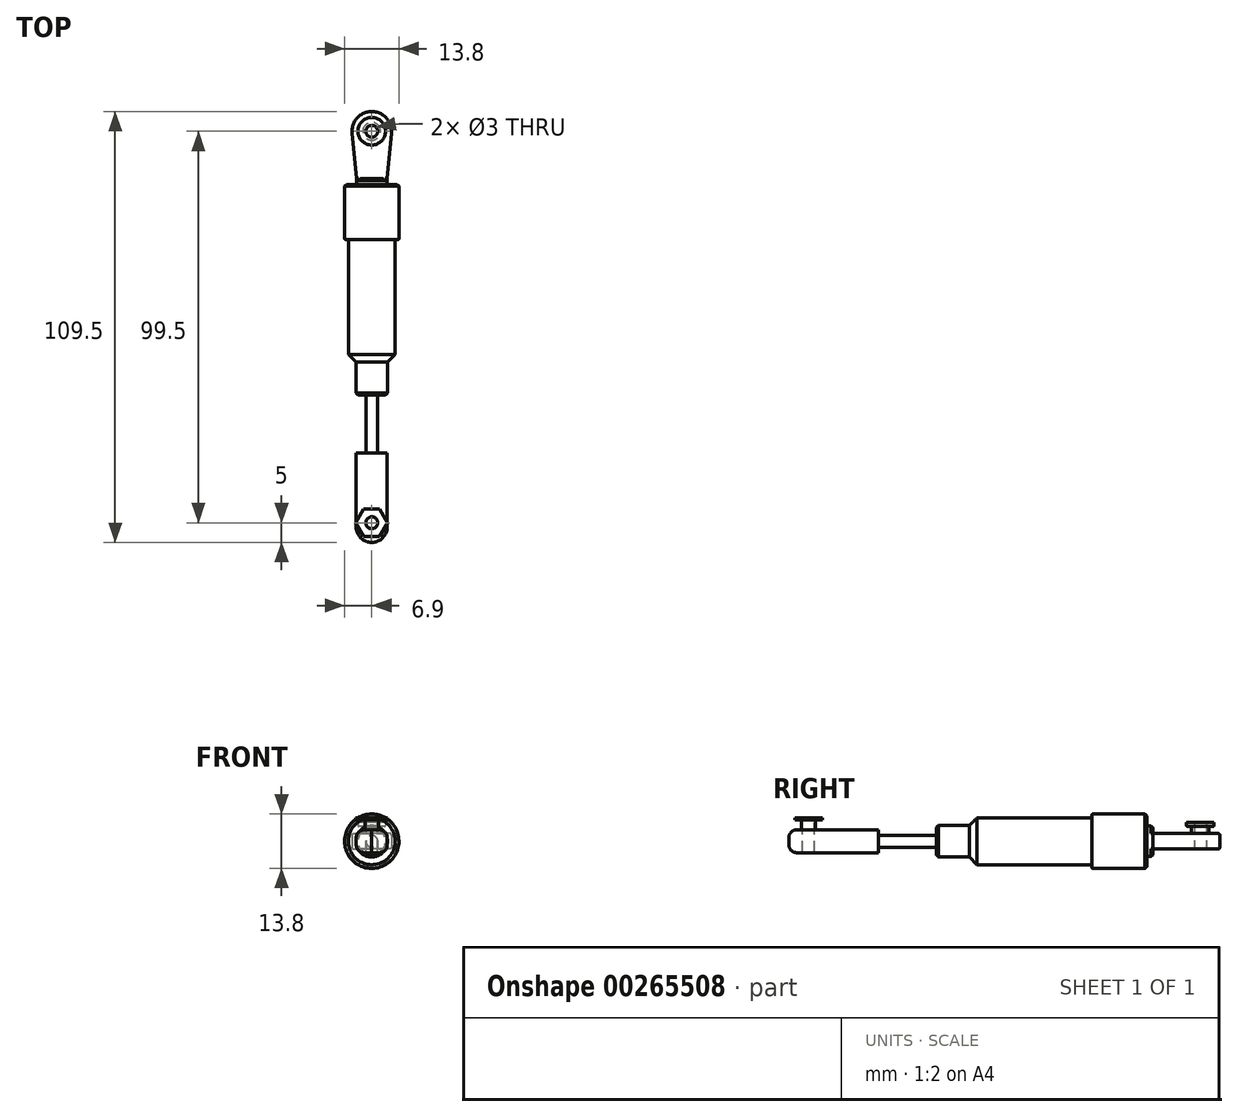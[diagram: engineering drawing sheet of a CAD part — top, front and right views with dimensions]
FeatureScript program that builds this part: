
annotation { "Feature Type Name" : "Feature", "Feature Type Description" : "" }
export const myFeature = defineFeature(function(context is Context, id is Id, definition is map)
    precondition{}
    {
        {
            var Q0;
            Q0=qCreatedBy(makeId("Front.planeOp"),FACE);
            var sketch = newSketch(context, id + "F0", { "sketchPlane" : qUnion([Q0])});
            skCircle(sketch, "E0", {"center": v(0, 0) * mm, "radius": 6.9 * mm});
            skSolve(sketch);
        }
        {
            var Q0;
            Q0=makeQuery(id+"F0.imprint","IMPRINT",FACE,{"disambiguationData":[TD([[makeQuery(id+"F0.imprint","IMPRINT",EDGE,{"derivedFrom":sQuery(id+"F0.wireOp",EDGE,"E0")}),1.0]])]});
            extrude(context, id + "F1", {"entities" : qUnion([Q0]), "depth" : 14 * mm});
        }
        {
            var Q0;
            Q0=makeQuery(id+"F1.opExtrude","CAP_FACE",FACE,{"disambiguationData":[OSD([sQuery(id+"F0.wireOp",EDGE,"E0")])],"isStart":false});
            var sketch = newSketch(context, id + "F2", { "sketchPlane" : qUnion([Q0])});
            skCircle(sketch, "E1", {"center": v(0, 0) * mm, "radius": 5.95 * mm});
            skSolve(sketch);
        }
        {
            var Q0;
            Q0=makeQuery(id+"F2.imprint","IMPRINT",FACE,{"disambiguationData":[TD([[makeQuery(id+"F2.imprint","IMPRINT",EDGE,{"derivedFrom":sQuery(id+"F2.wireOp",EDGE,"E1")}),1.0]])]});
            extrude(context, id + "F3", {"entities" : qUnion([Q0]), "operationType" : NewBodyOperationType.ADD, "depth" : 32 * mm});
        }
        {
            var Q0;
            Q0=makeQuery(id+"F3.opExtrude","CAP_FACE",FACE,{"disambiguationData":[OSD([sQuery(id+"F2.wireOp",EDGE,"E1")])],"isStart":false});
            var sketch = newSketch(context, id + "F4", { "sketchPlane" : qUnion([Q0])});
            skCircle(sketch, "E2", {"center": v(0, 0) * mm, "radius": 4 * mm});
            skSolve(sketch);
        }
        {
            var Q0;
            Q0=makeQuery(id+"F4.imprint","IMPRINT",FACE,{"disambiguationData":[TD([[makeQuery(id+"F4.imprint","IMPRINT",EDGE,{"derivedFrom":sQuery(id+"F4.wireOp",EDGE,"E2")}),1.0]])]});
            extrude(context, id + "F5", {"entities" : qUnion([Q0]), "operationType" : NewBodyOperationType.ADD, "depth" : 7.5 * mm});
        }
        {
            var Q0;
            Q0=makeQuery(id+"F3.opExtrude","CAP_EDGE",EDGE,{"disambiguationData":[OSD([sQuery(id+"F2.wireOp",EDGE,"E1")])],"isStart":false});
            chamfer(context, id + "F6", {"entities" : qUnion([Q0]), "width" : 2.8 * mm, "tangentPropagation" : true});
        }
        {
            var Q0;
            Q0=makeQuery(id+"F5.opExtrude","CAP_FACE",FACE,{"disambiguationData":[OSD([sQuery(id+"F4.wireOp",EDGE,"E2")])],"isStart":false});
            var sketch = newSketch(context, id + "F7", { "sketchPlane" : qUnion([Q0])});
            skCircle(sketch, "E3", {"center": v(0, 0) * mm, "radius": 1.5 * mm});
            skSolve(sketch);
        }
        {
            var Q0;
            Q0=makeQuery(id+"F7.imprint","IMPRINT",FACE,{"disambiguationData":[TD([[makeQuery(id+"F7.imprint","IMPRINT",EDGE,{"derivedFrom":sQuery(id+"F7.wireOp",EDGE,"E3")}),1.0]])]});
            extrude(context, id + "F8", {"entities" : qUnion([Q0]), "operationType" : NewBodyOperationType.ADD, "depth" : 14.8 * mm});
        }
        {
            var Q0;
            Q0=makeQuery(id+"F8.opExtrude","CAP_FACE",FACE,{"disambiguationData":[OSD([sQuery(id+"F7.wireOp",EDGE,"E3")])],"isStart":false});
            var sketch = newSketch(context, id + "F9", { "sketchPlane" : qUnion([Q0])});
            skLineSegment(sketch, "E4.bottom", {"start": v(-3.95, -2.9) * mm, "end": v(3.95, -2.9) * mm});
            skLineSegment(sketch, "E4.top", {"start": v(-3.95, 2.9) * mm, "end": v(3.95, 2.9) * mm});
            skLineSegment(sketch, "E4.left", {"start": v(-3.95, -2.9) * mm, "end": v(-3.95, 2.9) * mm});
            skLineSegment(sketch, "E4.right", {"start": v(3.95, -2.9) * mm, "end": v(3.95, 2.9) * mm});
            skPoint(sketch, "E4.middle", {"position": v(0, 0) * mm});
            skSolve(sketch);
        }
        {
            var Q0;
            Q0=makeQuery(id+"F9.imprint","IMPRINT",FACE,{"disambiguationData":[TD([[makeQuery(id+"F9.imprint","IMPRINT",EDGE,{"derivedFrom":sQuery(id+"F9.wireOp",EDGE,"E4.bottom")}),1.0]])]});
            var Q1;
            Q1=makeQuery(id+"F9.imprint","IMPRINT",FACE,{"disambiguationData":[TD([[makeQuery(id+"F9.imprint","IMPRINT",EDGE,{"derivedFrom":makeQuery(id+"F8.opExtrude","CAP_EDGE",EDGE,{"disambiguationData":[OSD([sQuery(id+"F7.wireOp",EDGE,"E3")])],"isStart":false})}),1.0]])]});
            extrude(context, id + "F10", {"entities" : qUnion([Q0, Q1]), "operationType" : NewBodyOperationType.ADD, "depth" : 22.7 * mm});
        }
        {
            var Q0;
            Q0=makeQuery(id+"F10.opExtrude","CAP_EDGE",EDGE,{"disambiguationData":[OSD([sQuery(id+"F9.wireOp",EDGE,"E4.left")])],"isStart":false});
            var Q1;
            Q1=makeQuery(id+"F10.opExtrude","CAP_EDGE",EDGE,{"disambiguationData":[OSD([sQuery(id+"F9.wireOp",EDGE,"E4.right")])],"isStart":false});
            fillet(context, id + "F11", {"entities" : qUnion([Q0, Q1]), "radius" : 4 * mm, "tangentPropagation" : true, "allowEdgeOverflow" : false});
        }
        {
            var Q0;
            Q0=makeQuery(id+"F10.opExtrude","SWEPT_EDGE",EDGE,{"disambiguationData":[OSD([sQuery(id+"F9.wireOp",EDGE,"E4.top"),sQuery(id+"F9.wireOp",EDGE,"E4.left")])]});
            var Q1;
            Q1=makeQuery(id+"F10.opExtrude","SWEPT_EDGE",EDGE,{"disambiguationData":[OSD([sQuery(id+"F9.wireOp",EDGE,"E4.top"),sQuery(id+"F9.wireOp",EDGE,"E4.right")])]});
            var Q2;
            Q2=makeQuery(id+"F10.opExtrude","SWEPT_EDGE",EDGE,{"disambiguationData":[OSD([sQuery(id+"F9.wireOp",EDGE,"E4.bottom"),sQuery(id+"F9.wireOp",EDGE,"E4.right")])]});
            var Q3;
            Q3=makeQuery(id+"F10.opExtrude","SWEPT_EDGE",EDGE,{"disambiguationData":[OSD([sQuery(id+"F9.wireOp",EDGE,"E4.bottom"),sQuery(id+"F9.wireOp",EDGE,"E4.left")])]});
            fillet(context, id + "F12", {"entities" : qUnion([Q0, Q1, Q2, Q3]), "radius" : 2 * mm, "tangentPropagation" : true, "allowEdgeOverflow" : false});
        }
        {
            var Q0;
            Q0=makeQuery(id+"F10.opExtrude","SWEPT_FACE",FACE,{"disambiguationData":[OSD([sQuery(id+"F9.wireOp",EDGE,"E4.top")])]});
            var sketch = newSketch(context, id + "F13", { "sketchPlane" : qUnion([Q0])});
            skLineSegment(sketch, "E5", {"start": v(0, -86) * mm, "end": v(0, -91) * mm, "construction": true});
            skCircle(sketch, "E6", {"center": v(0, -86) * mm, "radius": 1.5 * mm});
            skCircle(sketch, "E7", {"center": v(0, -86) * mm, "radius": 1.75 * mm});
            skSolve(sketch);
        }
        {
            var Q0;
            Q0=makeQuery(id+"F13.imprint","IMPRINT",FACE,{"disambiguationData":[TD([[makeQuery(id+"F13.imprint","IMPRINT",EDGE,{"derivedFrom":sQuery(id+"F13.wireOp",EDGE,"E6")}),1.0]])]});
            extrude(context, id + "F14", {"entities" : qUnion([Q0]), "operationType" : NewBodyOperationType.REMOVE, "oppositeDirection" : true, "depth" : 10 * mm});
        }
        {
            var Q0;
            Q0=makeQuery(id+"F13.imprint","IMPRINT",FACE,{"disambiguationData":[TD([[makeQuery(id+"F13.imprint","IMPRINT",EDGE,{"derivedFrom":sQuery(id+"F13.wireOp",EDGE,"E6")}),-1.0]])]});
            var Q1;
            Q1=sQuery(id+"F13.wireOp",EDGE,"E7");
            var Q2;
            Q2=sQuery(id+"F13.wireOp",EDGE,"E6");
            extrude(context, id + "F15", {"entities" : qUnion([Q0]), "operationType" : NewBodyOperationType.ADD, "surfaceEntities" : qUnion([Q1, Q2]), "depth" : 2.5 * mm});
        }
        {
            var Q0;
            Q0=makeQuery(id+"F15.opExtrude","CAP_FACE",FACE,{"disambiguationData":[OSD([sQuery(id+"F13.wireOp",EDGE,"E6"),sQuery(id+"F13.wireOp",EDGE,"E7")])],"isStart":false});
            var sketch = newSketch(context, id + "F16", { "sketchPlane" : qUnion([Q0])});
            skCircle(sketch, "E8.cCircle", {"center": v(0, -86) * mm, "radius": 3.5 * mm, "construction": true});
            skLineSegment(sketch, "E8.0", {"start": v(2.02, -89.5) * mm, "end": v(-2.02, -89.5) * mm});
            skLineSegment(sketch, "E8.1", {"start": v(-2.02, -89.5) * mm, "end": v(-4.04, -86) * mm});
            skLineSegment(sketch, "E8.2", {"start": v(-4.04, -86) * mm, "end": v(-2.02, -82.5) * mm});
            skLineSegment(sketch, "E8.3", {"start": v(-2.02, -82.5) * mm, "end": v(2.02, -82.5) * mm});
            skLineSegment(sketch, "E8.4", {"start": v(2.02, -82.5) * mm, "end": v(4.04, -86) * mm});
            skLineSegment(sketch, "E8.5", {"start": v(4.04, -86) * mm, "end": v(2.02, -89.5) * mm});
            skPoint(sketch, "E8.0.midPoint", {"position": v(0, -89.5) * mm});
            skCircle(sketch, "E9", {"center": v(0, -86) * mm, "radius": 1.5 * mm});
            skSolve(sketch);
        }
        {
            var Q0;
            Q0 = qSketchRegion(id + "F16", true);
            extrude(context, id + "F17", {"entities" : qUnion([Q0]), "operationType" : NewBodyOperationType.ADD, "depth" : 0.5 * mm});
        }
        {
            var Q0;
            Q0=makeQuery(id+"F1.opExtrude","CAP_FACE",FACE,{"disambiguationData":[OSD([sQuery(id+"F0.wireOp",EDGE,"E0")])],"isStart":true});
            var sketch = newSketch(context, id + "F18", { "sketchPlane" : qUnion([Q0])});
            skCircle(sketch, "E10", {"center": v(0, 0) * mm, "radius": 3.9 * mm});
            skSolve(sketch);
        }
        {
            var Q0;
            Q0=makeQuery(id+"F18.imprint","IMPRINT",FACE,{"disambiguationData":[TD([[makeQuery(id+"F18.imprint","IMPRINT",EDGE,{"derivedFrom":sQuery(id+"F18.wireOp",EDGE,"E10")}),1.0]])]});
            extrude(context, id + "F19", {"entities" : qUnion([Q0]), "operationType" : NewBodyOperationType.ADD, "depth" : 1.5 * mm});
        }
        {
            var Q0;
            Q0=qCreatedBy(makeId("Top.planeOp"),FACE);
            var sketch = newSketch(context, id + "F20", { "sketchPlane" : qUnion([Q0])});
            skLineSegment(sketch, "E11", {"start": v(0, 0) * mm, "end": v(0, 13.5) * mm, "construction": true});
            skCircle(sketch, "E12", {"center": v(0, 13.5) * mm, "radius": 5 * mm});
            skLineSegment(sketch, "E13.bottom", {"start": v(-3.9, 0) * mm, "end": v(3.9, 0) * mm});
            skLineSegment(sketch, "E13.top", {"start": v(-3.9, 1.5) * mm, "end": v(3.9, 1.5) * mm});
            skLineSegment(sketch, "E13.left", {"start": v(-3.9, 0) * mm, "end": v(-3.9, 1.5) * mm});
            skLineSegment(sketch, "E13.right", {"start": v(3.9, 0) * mm, "end": v(3.9, 1.5) * mm});
            skLineSegment(sketch, "E14", {"start": v(-3.9, 0) * mm, "end": v(3.9, 0) * mm, "construction": true});
            skLineSegment(sketch, "E15", {"start": v(-4.98, 13.03) * mm, "end": v(-3.9, 1.5) * mm});
            skLineSegment(sketch, "E16.MirrorCS", {"start": v(4.98, 13.03) * mm, "end": v(3.9, 1.5) * mm});
            skSolve(sketch);
        }
        {
            var Q0;
            {var subQ0=sQuery(id+"F20.wireOp",EDGE,"E12");var subQ1=makeQuery(id+"F20.imprint","INTERSECT",VERTEX,{"derivedFrom":[subQ0,sQuery(id+"F20.wireOp",EDGE,"E15")]});Q0=makeQuery(id+"F20.imprint","IMPRINT",FACE,{"disambiguationData":[TD([[makeQuery(id+"F20.imprint","IMPRINT",EDGE,{"disambiguationData":[TD([[subQ1,-1.0]])],"derivedFrom":subQ0}),1.0]])]});}
            var Q1;
            Q1=makeQuery(id+"F20.imprint","IMPRINT",FACE,{"disambiguationData":[TD([[makeQuery(id+"F20.imprint","IMPRINT",EDGE,{"derivedFrom":sQuery(id+"F20.wireOp",EDGE,"E13.top")}),1.0]])]});
            extrude(context, id + "F21", {"entities" : qUnion([Q0, Q1]), "operationType" : NewBodyOperationType.ADD, "depth" : 4 * mm, "symmetric" : true});
        }
        {
            var Q0;
            Q0=makeQuery(id+"F21.opExtrude","CAP_FACE",FACE,{"disambiguationData":[OSD([sQuery(id+"F20.wireOp",EDGE,"E12"),sQuery(id+"F20.wireOp",EDGE,"E13.top"),sQuery(id+"F20.wireOp",EDGE,"E15"),sQuery(id+"F20.wireOp",EDGE,"E16.MirrorCS")])],"isStart":false});
            var sketch = newSketch(context, id + "F22", { "sketchPlane" : qUnion([Q0])});
            skCircle(sketch, "E17", {"center": v(0, 13.5) * mm, "radius": 1.5 * mm});
            skCircle(sketch, "E18", {"center": v(0, 13.5) * mm, "radius": 2.25 * mm});
            skSolve(sketch);
        }
        {
            var Q0;
            Q0=makeQuery(id+"F22.imprint","IMPRINT",FACE,{"disambiguationData":[TD([[makeQuery(id+"F22.imprint","IMPRINT",EDGE,{"derivedFrom":sQuery(id+"F22.wireOp",EDGE,"E17")}),-1.0]])]});
            extrude(context, id + "F23", {"entities" : qUnion([Q0]), "operationType" : NewBodyOperationType.ADD, "depth" : 1.8 * mm});
        }
        {
            var Q0;
            Q0=makeQuery(id+"F23.boolean.opBoolean","SPLIT",FACE,{"disambiguationData":[TD([makeQuery(id+"F23.opExtrude","SWEPT_FACE",FACE,{"disambiguationData":[OSD([sQuery(id+"F22.wireOp",EDGE,"E17")])]})])],"derivedFrom":makeQuery(id+"F21.opExtrude","CAP_FACE",FACE,{"disambiguationData":[OSD([sQuery(id+"F20.wireOp",EDGE,"E12"),sQuery(id+"F20.wireOp",EDGE,"E13.top"),sQuery(id+"F20.wireOp",EDGE,"E15"),sQuery(id+"F20.wireOp",EDGE,"E16.MirrorCS")])],"isStart":false})});
            extrude(context, id + "F24", {"entities" : qUnion([Q0]), "operationType" : NewBodyOperationType.REMOVE, "oppositeDirection" : true, "depth" : 5 * mm});
        }
        {
            var Q0;
            Q0=makeQuery(id+"F23.opExtrude","CAP_FACE",FACE,{"disambiguationData":[OSD([sQuery(id+"F22.wireOp",EDGE,"E17"),sQuery(id+"F22.wireOp",EDGE,"E18")])],"isStart":false});
            var sketch = newSketch(context, id + "F25", { "sketchPlane" : qUnion([Q0])});
            skCircle(sketch, "E19", {"center": v(0, 13.5) * mm, "radius": 3.5 * mm});
            skCircle(sketch, "E20", {"center": v(0, 13.5) * mm, "radius": 1.5 * mm});
            skSolve(sketch);
        }
        {
            var Q0;
            Q0 = qSketchRegion(id + "F25", true);
            extrude(context, id + "F26", {"entities" : qUnion([Q0]), "operationType" : NewBodyOperationType.ADD, "depth" : 1 * mm});
        }
        {
            var Q0;
            Q0=makeQuery(id+"F5.opExtrude","CAP_EDGE",EDGE,{"disambiguationData":[OSD([sQuery(id+"F4.wireOp",EDGE,"E2")])],"isStart":false});
            var Q1;
            Q1=makeQuery(id+"F1.opExtrude","CAP_EDGE",EDGE,{"disambiguationData":[OSD([sQuery(id+"F0.wireOp",EDGE,"E0")])],"isStart":true});
            var Q2;
            {var subQ0=sQuery(id+"F18.wireOp",EDGE,"E10");var subQ1=makeQuery(id+"F19.opExtrude","SWEPT_FACE",FACE,{"disambiguationData":[OSD([subQ0])]});var subQ2=makeQuery(id+"F19.opExtrude","CAP_FACE",FACE,{"disambiguationData":[OSD([subQ0])],"isStart":false});var subQ3=sQuery(id+"F20.wireOp",EDGE,"E13.top");Q2=makeQuery(id+"F21.boolean.opBoolean","SPLIT",EDGE,{"disambiguationData":[topologyDisambiguationEdgeConnected([subQ1,subQ2]),TD([makeQuery(id+"F21.opExtrude","CAP_FACE",FACE,{"disambiguationData":[OSD([sQuery(id+"F20.wireOp",EDGE,"E12"),subQ3,sQuery(id+"F20.wireOp",EDGE,"E15"),sQuery(id+"F20.wireOp",EDGE,"E16.MirrorCS")])],"isStart":false})])],"derivedFrom":makeQuery(id+"F19.opExtrude","CAP_EDGE",EDGE,{"disambiguationData":[OSD([subQ0])],"isStart":false})});}
            var Q3;
            {var subQ0=sQuery(id+"F18.wireOp",EDGE,"E10");var subQ1=makeQuery(id+"F19.opExtrude","SWEPT_FACE",FACE,{"disambiguationData":[OSD([subQ0])]});var subQ2=sQuery(id+"F20.wireOp",EDGE,"E13.top");var subQ3=makeQuery(id+"F19.opExtrude","CAP_FACE",FACE,{"disambiguationData":[OSD([subQ0])],"isStart":false});Q3=makeQuery(id+"F21.boolean.opBoolean","SPLIT",EDGE,{"disambiguationData":[topologyDisambiguationEdgeConnected([subQ1,subQ3]),TD([makeQuery(id+"F21.opExtrude","CAP_FACE",FACE,{"disambiguationData":[OSD([sQuery(id+"F20.wireOp",EDGE,"E12"),subQ2,sQuery(id+"F20.wireOp",EDGE,"E15"),sQuery(id+"F20.wireOp",EDGE,"E16.MirrorCS")])],"isStart":true})])],"derivedFrom":makeQuery(id+"F19.opExtrude","CAP_EDGE",EDGE,{"disambiguationData":[OSD([subQ0])],"isStart":false})});}
            chamfer(context, id + "F27", {"entities" : qUnion([Q0, Q1, Q2, Q3]), "width" : 0.5 * mm, "tangentPropagation" : true});
        }
        {
            var Q0;
            Q0=makeQuery(id+"F1.opExtrude","CAP_EDGE",EDGE,{"disambiguationData":[OSD([sQuery(id+"F0.wireOp",EDGE,"E0")])],"isStart":false});
            fillet(context, id + "F28", {"entities" : qUnion([Q0]), "radius" : 0.2 * mm, "tangentPropagation" : true, "allowEdgeOverflow" : false});
        }
        {
            var Q0;
            Q0=makeQuery(id+"F21.opExtrude","CAP_EDGE",EDGE,{"disambiguationData":[OSD([sQuery(id+"F20.wireOp",EDGE,"E16.MirrorCS")])],"isStart":false});
            var Q1;
            Q1=makeQuery(id+"F21.opExtrude","CAP_EDGE",EDGE,{"disambiguationData":[OSD([sQuery(id+"F20.wireOp",EDGE,"E12")])],"isStart":false});
            var Q2;
            Q2=makeQuery(id+"F21.opExtrude","CAP_EDGE",EDGE,{"disambiguationData":[OSD([sQuery(id+"F20.wireOp",EDGE,"E15")])],"isStart":false});
            var Q3;
            Q3=makeQuery(id+"F21.opExtrude","CAP_EDGE",EDGE,{"disambiguationData":[OSD([sQuery(id+"F20.wireOp",EDGE,"E12")])],"isStart":true});
            var Q4;
            Q4=makeQuery(id+"F21.opExtrude","CAP_EDGE",EDGE,{"disambiguationData":[OSD([sQuery(id+"F20.wireOp",EDGE,"E15")])],"isStart":true});
            var Q5;
            Q5=makeQuery(id+"F21.opExtrude","CAP_EDGE",EDGE,{"disambiguationData":[OSD([sQuery(id+"F20.wireOp",EDGE,"E16.MirrorCS")])],"isStart":true});
            fillet(context, id + "F29", {"entities" : qUnion([Q0, Q1, Q2, Q3, Q4, Q5]), "radius" : 0.5 * mm, "tangentPropagation" : true, "allowEdgeOverflow" : false});
        }
        {
            var Q0;
            Q0=makeQuery(id+"F26.opExtrude","CAP_EDGE",EDGE,{"disambiguationData":[OSD([sQuery(id+"F25.wireOp",EDGE,"E19")])],"isStart":true});
            fillet(context, id + "F30", {"entities" : qUnion([Q0]), "radius" : 0.2 * mm, "tangentPropagation" : true, "allowEdgeOverflow" : false});
        }
    });
